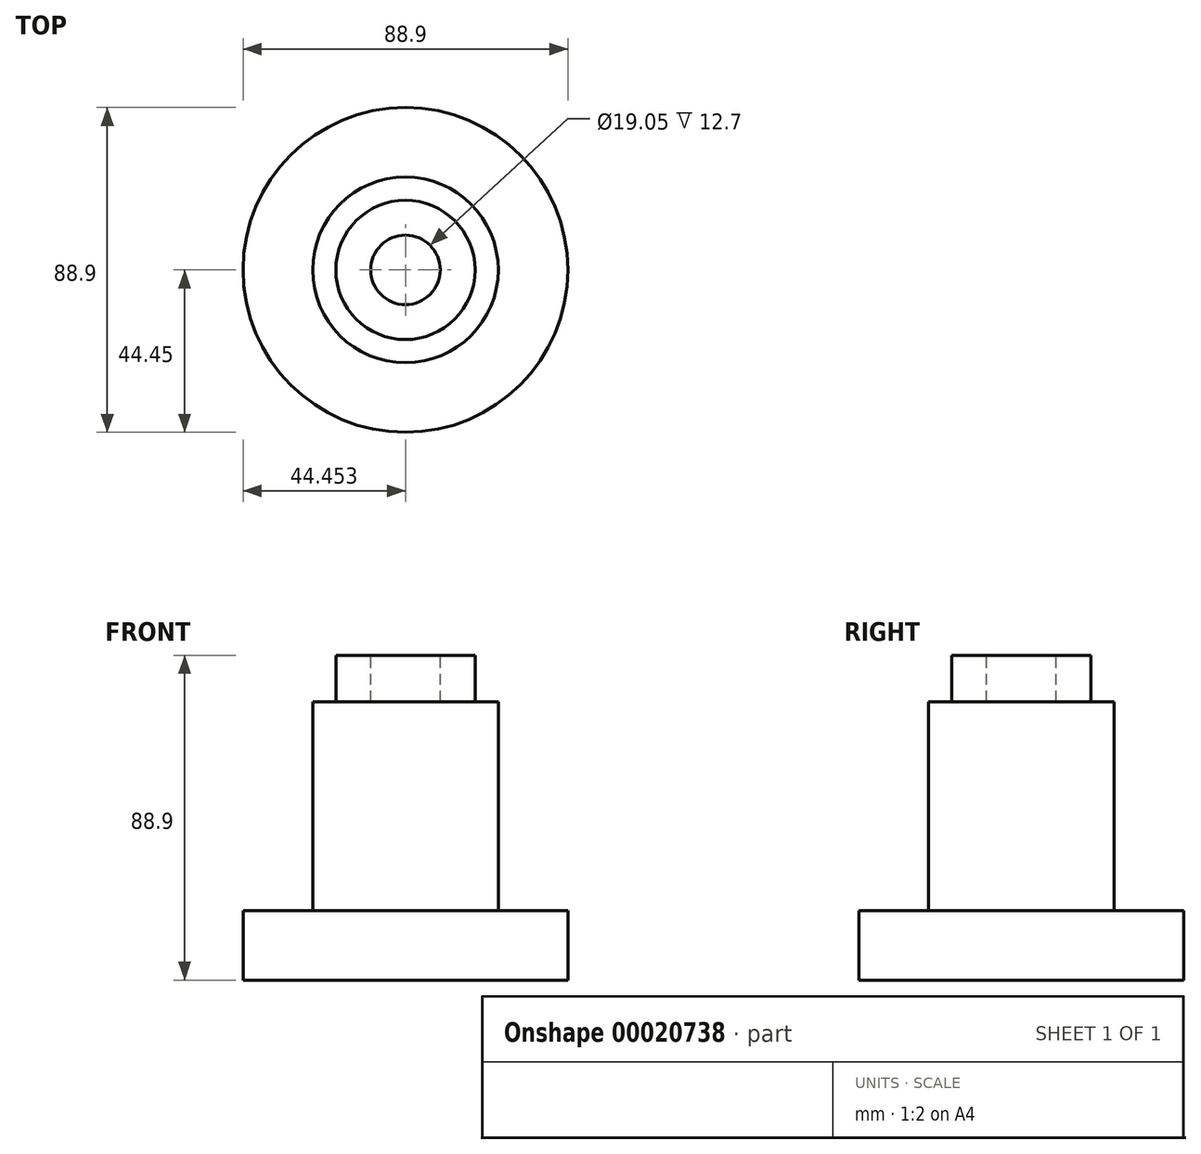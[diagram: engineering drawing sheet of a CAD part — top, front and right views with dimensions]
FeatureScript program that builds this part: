
annotation { "Feature Type Name" : "Feature", "Feature Type Description" : "" }
export const myFeature = defineFeature(function(context is Context, id is Id, definition is map)
    precondition{}
    {
        {
            var Q0;
            Q0=qCreatedBy(makeId("Front.planeOp"),FACE);
            var sketch = newSketch(context, id + "F0", { "sketchPlane" : qUnion([Q0])});
            skLineSegment(sketch, "E0.bottom", {"start": v(0.24, 45.44) * mm, "end": v(9.76, 45.44) * mm});
            skLineSegment(sketch, "E0.top", {"start": v(-9.29, -43.46) * mm, "end": v(35.16, -43.46) * mm});
            skLineSegment(sketch, "E0.left", {"start": v(-9.29, 32.74) * mm, "end": v(-9.29, -43.46) * mm});
            skLineSegment(sketch, "E0.right", {"start": v(35.16, -24.4) * mm, "end": v(35.16, -43.46) * mm});
            skLineSegment(sketch, "E1", {"start": v(16.11, 32.74) * mm, "end": v(16.11, -24.4) * mm});
            skLineSegment(sketch, "E2", {"start": v(16.11, -24.4) * mm, "end": v(35.16, -24.4) * mm});
            skLineSegment(sketch, "E3", {"start": v(9.76, 45.44) * mm, "end": v(9.76, 32.74) * mm});
            skLineSegment(sketch, "E4", {"start": v(9.76, 32.74) * mm, "end": v(16.11, 32.74) * mm});
            skPoint(sketch, "E5.orphan", {"position": v(16.11, 45.44) * mm});
            skPoint(sketch, "E6", {"position": v(0.24, 45.44) * mm});
            skLineSegment(sketch, "E7", {"start": v(0.24, 45.44) * mm, "end": v(0.24, 32.74) * mm});
            skLineSegment(sketch, "E8", {"start": v(0.24, 32.74) * mm, "end": v(-9.29, 32.74) * mm});
            skPoint(sketch, "E9.orphan", {"position": v(-9.29, 45.44) * mm});
            skSolve(sketch);
        }
        {
            var Q0;
            Q0=makeQuery(id+"F0.imprint","IMPRINT",FACE,{"disambiguationData":[TD([[makeQuery(id+"F0.imprint","IMPRINT",EDGE,{"derivedFrom":sQuery(id+"F0.wireOp",EDGE,"E0.bottom")}),-1.0]])]});
            var Q1;
            Q1=sQuery(id+"F0.wireOp",EDGE,"E0.left");
            revolve(context, id + "F1", {"entities" : qUnion([Q0]), "axis" : qUnion([Q1]), "revolveType" : RevolveType.FULL});
        }
    });
